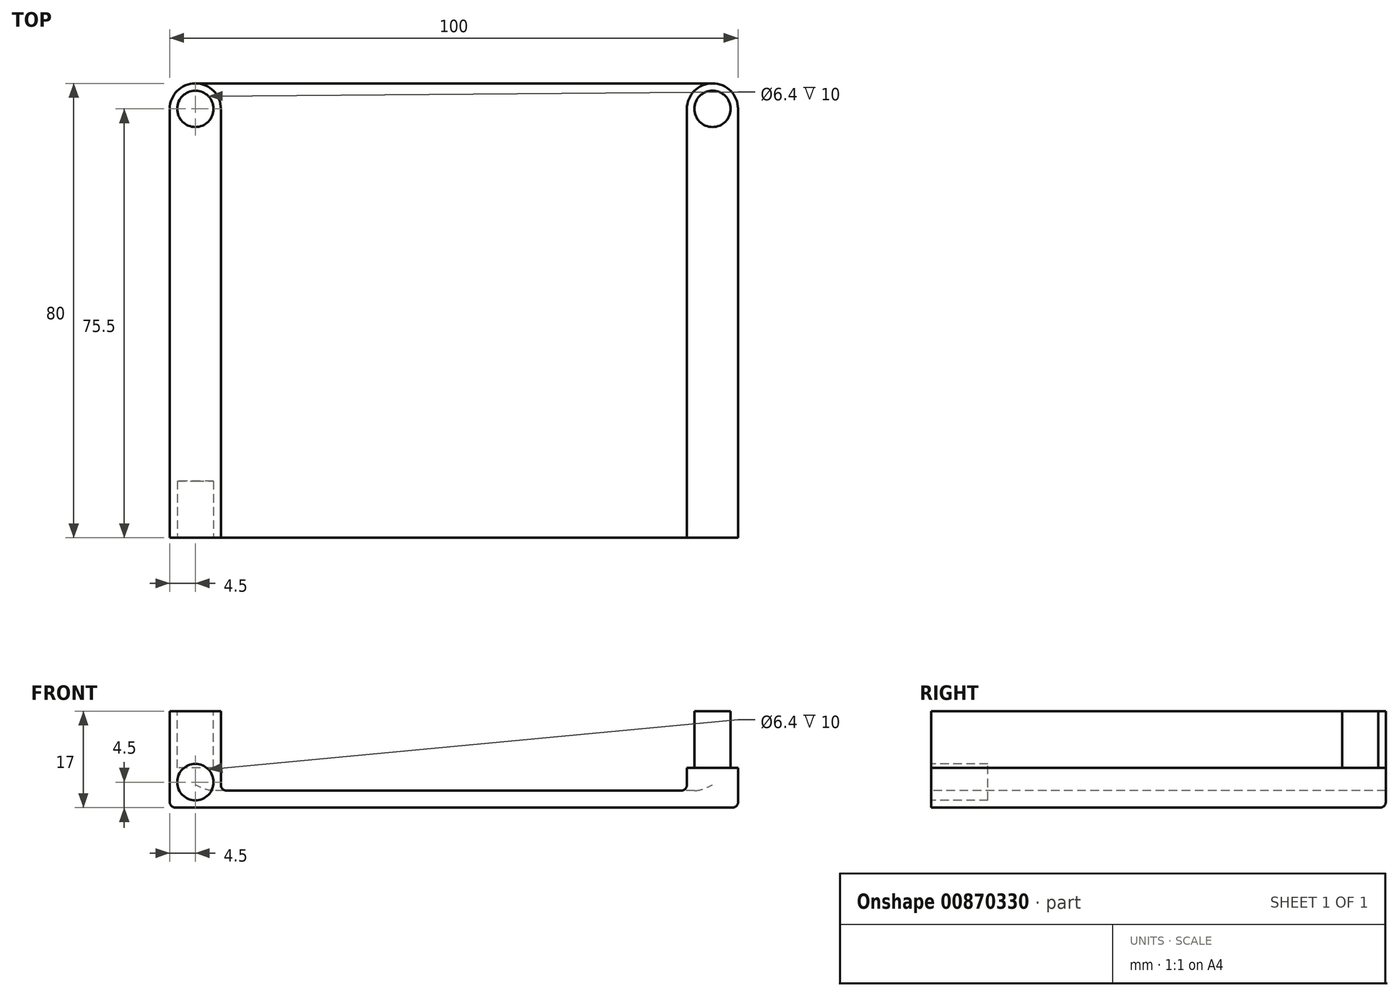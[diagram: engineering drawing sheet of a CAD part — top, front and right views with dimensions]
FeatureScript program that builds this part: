
annotation { "Feature Type Name" : "Feature", "Feature Type Description" : "" }
export const myFeature = defineFeature(function(context is Context, id is Id, definition is map)
    precondition{}
    {
        {
            var Q0;
            Q0=qCreatedBy(makeId("Top.planeOp"),FACE);
            var sketch = newSketch(context, id + "F0", { "sketchPlane" : qUnion([Q0])});
            skLineSegment(sketch, "E0.bottom", {"start": v(0, 0) * mm, "end": v(50, 0) * mm});
            skLineSegment(sketch, "E0.top", {"start": v(4.5, 80) * mm, "end": v(50, 80) * mm});
            skLineSegment(sketch, "E0.left", {"start": v(0, 0) * mm, "end": v(0, 75.5) * mm});
            skLineSegment(sketch, "E0.right", {"start": v(50, 0) * mm, "end": v(50, 80) * mm, "construction": true});
            skPoint(sketch, "E1.visualSharp", {"position": v(0, 80) * mm});
            skArc(sketch, "E1.filletArc", {"start": v(4.5, 80) * mm, "mid": v(1.32, 78.68) * mm, "end": v(0, 75.5) * mm});
            skArc(sketch, "E2.MirrorCS", {"start": v(95.5, 80) * mm, "mid": v(98.68, 78.68) * mm, "end": v(100, 75.5) * mm});
            skPoint(sketch, "E3.MirrorP", {"position": v(100, 80) * mm});
            skLineSegment(sketch, "E4.MirrorCS", {"start": v(95.5, 80) * mm, "end": v(50, 80) * mm});
            skLineSegment(sketch, "E5.MirrorCS", {"start": v(100, 0) * mm, "end": v(100, 75.5) * mm});
            skLineSegment(sketch, "E6.MirrorCS", {"start": v(100, 0) * mm, "end": v(50, 0) * mm});
            skSolve(sketch);
        }
        {
            var Q0;
            Q0=qCreatedBy(makeId("Top.planeOp"),FACE);
            cPlane(context, id + "F1", {"entities" : qUnion([Q0]), "cplaneType" : CPlaneType.OFFSET, "offset" : 17 * mm, "width" : 150 * mm, "height" : 150 * mm});
        }
        {
            var Q0;
            Q0=makeQuery(id+"F0.imprint","IMPRINT",FACE,{"disambiguationData":[TD([[makeQuery(id+"F0.imprint","IMPRINT",EDGE,{"derivedFrom":sQuery(id+"F0.wireOp",EDGE,"E0.bottom")}),1.0]])]});
            extrude(context, id + "F2", {"entities" : qUnion([Q0]), "depth" : 17 * mm, "offsetDistance" : 25 * mm});
        }
        {
            var Q0;
            Q0=qCreatedBy(id+"F1.planeOp",FACE);
            var sketch = newSketch(context, id + "F3", { "sketchPlane" : qUnion([Q0])});
            skLineSegment(sketch, "E7.bottom", {"start": v(0, 0) * mm, "end": v(50, 0) * mm});
            skLineSegment(sketch, "E7.top", {"start": v(4.5, 80) * mm, "end": v(50, 80) * mm});
            skLineSegment(sketch, "E7.left", {"start": v(0, 0) * mm, "end": v(0, 75.5) * mm});
            skLineSegment(sketch, "E7.right", {"start": v(50, 0) * mm, "end": v(50, 80) * mm, "construction": true});
            skLineSegment(sketch, "E8", {"start": v(4.5, 99.58) * mm, "end": v(4.5, -15.56) * mm, "construction": true});
            skLineSegment(sketch, "E9", {"start": v(9, 100.07) * mm, "end": v(9, -16.86) * mm, "construction": true});
            skLineSegment(sketch, "E10", {"start": v(18, 99.9) * mm, "end": v(18, -19.31) * mm, "construction": true});
            skCircle(sketch, "E11", {"center": v(4.5, 75.5) * mm, "radius": 3.2 * mm});
            skPoint(sketch, "E12.visualSharp", {"position": v(0, 80) * mm});
            skArc(sketch, "E12.filletArc", {"start": v(4.5, 80) * mm, "mid": v(1.32, 78.68) * mm, "end": v(0, 75.5) * mm});
            skLineSegment(sketch, "E13", {"start": v(9, 75.5) * mm, "end": v(9, 0) * mm});
            skLineSegment(sketch, "E14", {"start": v(4.5, 80) * mm, "end": v(4.5, 80) * mm});
            skPoint(sketch, "E15.visualSharp", {"position": v(9, 80) * mm});
            skArc(sketch, "E15.filletArc", {"start": v(9, 75.5) * mm, "mid": v(7.68, 78.68) * mm, "end": v(4.5, 80) * mm});
            skLineSegment(sketch, "E16.MirrorCS", {"start": v(95.5, 80) * mm, "end": v(95.5, 80) * mm});
            skPoint(sketch, "E17.MirrorP", {"position": v(100, 80) * mm});
            skCircle(sketch, "E18.MirrorC", {"center": v(95.5, 75.5) * mm, "radius": 3.2 * mm});
            skArc(sketch, "E19.MirrorCS", {"start": v(91, 75.5) * mm, "mid": v(92.32, 78.68) * mm, "end": v(95.5, 80) * mm});
            skPoint(sketch, "E20.MirrorP", {"position": v(91, 80) * mm});
            skArc(sketch, "E21.MirrorCS", {"start": v(95.5, 80) * mm, "mid": v(98.68, 78.68) * mm, "end": v(100, 75.5) * mm});
            skLineSegment(sketch, "E22.MirrorCS", {"start": v(100, 0) * mm, "end": v(100, 75.5) * mm});
            skLineSegment(sketch, "E23.MirrorCS", {"start": v(100, 0) * mm, "end": v(50, 0) * mm});
            skLineSegment(sketch, "E24.MirrorCS", {"start": v(95.5, 80) * mm, "end": v(50, 80) * mm});
            skLineSegment(sketch, "E25.MirrorCS", {"start": v(91, 75.5) * mm, "end": v(91, 0) * mm});
            skSolve(sketch);
        }
        {
            var Q0;
            Q0=makeQuery(id+"F3.imprint","IMPRINT",FACE,{"disambiguationData":[TD([[makeQuery(id+"F3.imprint","IMPRINT",EDGE,{"derivedFrom":sQuery(id+"F3.wireOp",EDGE,"E7.top")}),-1.0]])]});
            extrude(context, id + "F4", {"entities" : qUnion([Q0]), "operationType" : NewBodyOperationType.REMOVE, "oppositeDirection" : true, "depth" : 14 * mm, "offsetDistance" : 25 * mm});
        }
        {
            var Q0;
            Q0=makeQuery(id+"F3.imprint","IMPRINT",FACE,{"disambiguationData":[TD([[makeQuery(id+"F3.imprint","IMPRINT",EDGE,{"derivedFrom":sQuery(id+"F3.wireOp",EDGE,"E11")}),1.0]])]});
            var Q1;
            Q1=makeQuery(id+"F3.imprint","IMPRINT",FACE,{"disambiguationData":[TD([[makeQuery(id+"F3.imprint","IMPRINT",EDGE,{"derivedFrom":sQuery(id+"F3.wireOp",EDGE,"E18.MirrorC")}),-1.0]])]});
            extrude(context, id + "F5", {"entities" : qUnion([Q0, Q1]), "operationType" : NewBodyOperationType.REMOVE, "oppositeDirection" : true, "depth" : 10 * mm, "offsetDistance" : 25 * mm});
        }
        {
            var Q0;
            Q0=qCreatedBy(makeId("Front.planeOp"),FACE);
            var sketch = newSketch(context, id + "F6", { "sketchPlane" : qUnion([Q0])});
            skLineSegment(sketch, "E26", {"start": v(50, 39.58) * mm, "end": v(50, -24.46) * mm, "construction": true});
            skCircle(sketch, "E27", {"center": v(4.5, 4.5) * mm, "radius": 3.2 * mm});
            skCircle(sketch, "E28.MirrorC", {"center": v(95.5, 4.5) * mm, "radius": 3.2 * mm});
            skSolve(sketch);
        }
        {
            var Q0;
            Q0=makeQuery(id+"F6.imprint","IMPRINT",FACE,{"disambiguationData":[TD([[makeQuery(id+"F6.imprint","IMPRINT",EDGE,{"derivedFrom":sQuery(id+"F6.wireOp",EDGE,"E27")}),1.0]])]});
            var Q1;
            Q1=makeQuery(id+"F6.imprint","IMPRINT",FACE,{"disambiguationData":[TD([[makeQuery(id+"F6.imprint","IMPRINT",EDGE,{"derivedFrom":sQuery(id+"F6.wireOp",EDGE,"E28.MirrorC")}),-1.0]])]});
            extrude(context, id + "F7", {"entities" : qUnion([Q0, Q1]), "operationType" : NewBodyOperationType.REMOVE, "oppositeDirection" : true, "depth" : 10 * mm, "offsetDistance" : 25 * mm});
        }
        {
            var Q0;
            Q0=makeQuery(id+"F4.boolean.opBoolean","COPY",EDGE,{"derivedFrom":makeQuery(id+"F4.opExtrude","CAP_EDGE",EDGE,{"disambiguationData":[OSD([sQuery(id+"F3.wireOp",EDGE,"E13")])],"isStart":false})});
            var Q1;
            Q1=makeQuery(id+"F4.boolean.opBoolean","COPY",EDGE,{"derivedFrom":makeQuery(id+"F4.opExtrude","CAP_EDGE",EDGE,{"disambiguationData":[OSD([sQuery(id+"F3.wireOp",EDGE,"E25.MirrorCS")])],"isStart":false})});
            var Q2;
            Q2=makeQuery(id+"F4.boolean.opBoolean","COPY",EDGE,{"derivedFrom":makeQuery(id+"F4.opExtrude","CAP_EDGE",EDGE,{"disambiguationData":[OSD([sQuery(id+"F3.wireOp",EDGE,"E7.top"),sQuery(id+"F3.wireOp",EDGE,"E24.MirrorCS")])],"isStart":false})});
            var Q3;
            Q3=makeQuery(id+"F2.opExtrude","CAP_EDGE",EDGE,{"disambiguationData":[OSD([sQuery(id+"F0.wireOp",EDGE,"E0.top"),sQuery(id+"F0.wireOp",EDGE,"E4.MirrorCS")])],"isStart":true});
            var Q4;
            Q4=makeQuery(id+"F4.boolean.opBoolean","COPY",EDGE,{"derivedFrom":makeQuery(id+"F4.opExtrude","CAP_EDGE",EDGE,{"disambiguationData":[OSD([sQuery(id+"F3.wireOp",EDGE,"E13")])],"isStart":true})});
            var Q5;
            Q5=makeQuery(id+"F4.boolean.opBoolean","COPY",EDGE,{"derivedFrom":makeQuery(id+"F4.opExtrude","CAP_EDGE",EDGE,{"disambiguationData":[OSD([sQuery(id+"F3.wireOp",EDGE,"E25.MirrorCS")])],"isStart":true})});
            var Q6;
            Q6=makeQuery(id+"F5.boolean.opBoolean","COPY",EDGE,{"derivedFrom":makeQuery(id+"F5.opExtrude","CAP_EDGE",EDGE,{"disambiguationData":[OSD([sQuery(id+"F3.wireOp",EDGE,"E11")])],"isStart":true})});
            var Q7;
            Q7=makeQuery(id+"F5.boolean.opBoolean","COPY",EDGE,{"derivedFrom":makeQuery(id+"F5.opExtrude","CAP_EDGE",EDGE,{"disambiguationData":[OSD([sQuery(id+"F3.wireOp",EDGE,"E18.MirrorC")])],"isStart":true})});
            var Q8;
            Q8=makeQuery(id+"F7.boolean.opBoolean","COPY",EDGE,{"derivedFrom":makeQuery(id+"F7.opExtrude","CAP_EDGE",EDGE,{"disambiguationData":[OSD([sQuery(id+"F6.wireOp",EDGE,"E28.MirrorC")])],"isStart":true})});
            var Q9;
            Q9=makeQuery(id+"F7.boolean.opBoolean","COPY",EDGE,{"derivedFrom":makeQuery(id+"F7.opExtrude","CAP_EDGE",EDGE,{"disambiguationData":[OSD([sQuery(id+"F6.wireOp",EDGE,"E27")])],"isStart":true})});
            fillet(context, id + "F8", {"entities" : qUnion([Q0, Q1, Q2, Q3, Q4, Q5, Q6, Q7, Q8, Q9]), "radius" : 1 * mm, "tangentPropagation" : true, "allowEdgeOverflow" : false});
        }
    });
